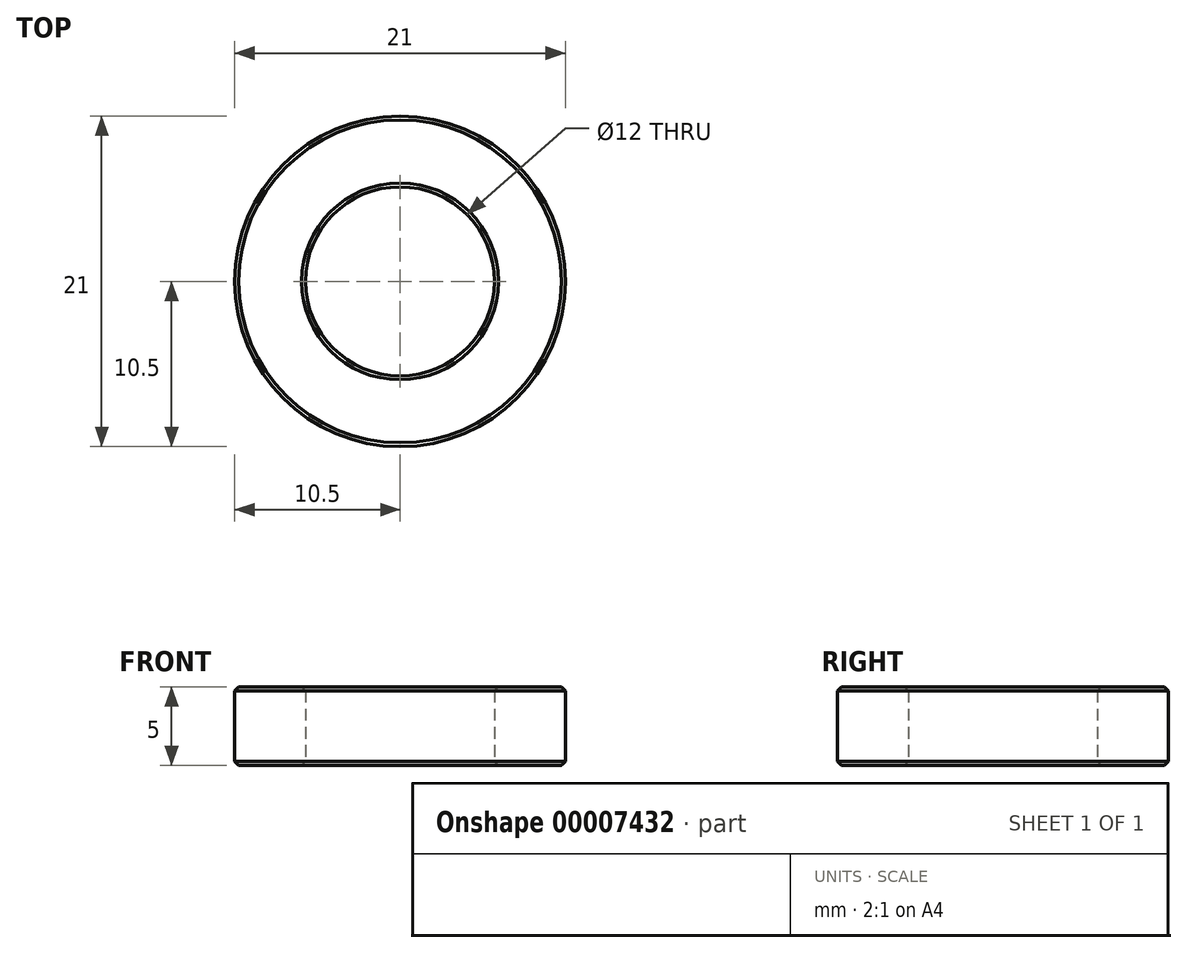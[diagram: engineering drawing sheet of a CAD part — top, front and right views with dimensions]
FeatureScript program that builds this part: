
annotation { "Feature Type Name" : "Feature", "Feature Type Description" : "" }
export const myFeature = defineFeature(function(context is Context, id is Id, definition is map)
    precondition{}
    {
        {
            var Q0;
            Q0=qCreatedBy(makeId("Top.planeOp"),FACE);
            var sketch = newSketch(context, id + "F0", { "sketchPlane" : qUnion([Q0])});
            skCircle(sketch, "E0", {"center": v(0, 0) * mm, "radius": 10.5 * mm});
            skCircle(sketch, "E1", {"center": v(0, 0) * mm, "radius": 6 * mm});
            skSolve(sketch);
        }
        {
            var Q0;
            Q0=makeQuery(id+"F0.imprint","IMPRINT",FACE,{"disambiguationData":[TD([[makeQuery(id+"F0.imprint","IMPRINT",EDGE,{"derivedFrom":sQuery(id+"F0.wireOp",EDGE,"E0")}),1.0]])]});
            extrude(context, id + "F1", {"entities" : qUnion([Q0]), "depth" : 5 * mm});
        }
        {
            var Q0;
            Q0=makeQuery(id+"F1.opExtrude","CAP_FACE",FACE,{"disambiguationData":[OSD([sQuery(id+"F0.wireOp",EDGE,"E0"),sQuery(id+"F0.wireOp",EDGE,"E1")])],"isStart":false});
            var Q1;
            Q1=makeQuery(id+"F1.opExtrude","CAP_FACE",FACE,{"disambiguationData":[OSD([sQuery(id+"F0.wireOp",EDGE,"E0"),sQuery(id+"F0.wireOp",EDGE,"E1")])],"isStart":true});
            chamfer(context, id + "F2", {"entities" : qUnion([Q0, Q1]), "width" : .25 * mm, "tangentPropagation" : true});
        }
    });
